# Revit family: ElectricalFixtures_WiringAccessories_Hager_Sollysta_FanIsolatorSwitches
name_source: partatom
category: Lighting Fixtures
revit_build: Autodesk Revit 2015 (Build: 20160512_1515(x64)
units: mm (PartAtom-declared; Revit-internal decimal feet)

## types (3) — shared parameters
CE Approval = Yes
Colour = SollystaWhite
Design Country = China
Expected Life = 25
Finish = Gloss
Frequency = 50/60Hz
Manufacturer = Hager
Manufacturer Country = UnitedKingdom
Manufacturer Website = http://www.hager.co.uk
Material = Urea Formaldehyde Thermoset Plastic
Overall Depth = 50 mm  [stored 0.164042 ft]
Overall Width = 100 mm  [stored 0.328084 ft]
Packaging Recyclable = Yes
Product Family = WhiteMouldedCeilingSwitches
Product Group = FanIsolatorSwitches
Product Literature = http://www.hager.co.uk
Product Range = WhiteMouldedCeilingSwitches_FanIsolatorSwitches
Product URL = http://www.hager.co.uk
Reference Standard = BS 1363-2
Shape = Circular
Supply Phase = 1
Type = ElectricalFixture
URL = http://www.hager.co.uk
Voltage (Volts) = 230V/240V
zero-valued in all types: Overall Height

## per-type parameters (varying)
| type | Description | EAN Code | Features | Name | Technical Description |
| WMCS3PIF | 10A3PCeilingSwitchMarkedFan&Isolator | 5015652260219 | 10A3PCeilingSwitchMarkedFan&Isolator | WhiteMouldedCeilingSwitches_FanIsolatorSwitches_WMCS3PIF | 10A3PCeilingSwitchMarkedFan&Isolator |
| WMCS3PI | 10A3PCeilingSwitchMarkedIsolator | 5015652260202 | 10A3PCeilingSwitchMarkedIsolator | WhiteMouldedCeilingSwitches_FanIsolatorSwitches_WMCS3PI | 10A3PCeilingSwitchMarkedIsolator |
| WMCS3PF | 10A3PCeilingSwitchMarkedIsolator | 5015652260202 | 10A3PCeilingSwitchMarkedIsolator | WhiteMouldedCeilingSwitches_FanIsolatorSwitches_WMCS3PF | 10A3PCeilingSwitchMarkedIsolator |

note: column(s) folded — value = type name in every type: Product Model Number, Unique Reference

note: [stored X ft] marks values corroborated as IEEE doubles in the binary element streams (Revit-internal decimal feet)

## geometry (parser evidence)
native form markers: Blend x4, Sweep x1
no freeform markers — native parametric forms only
